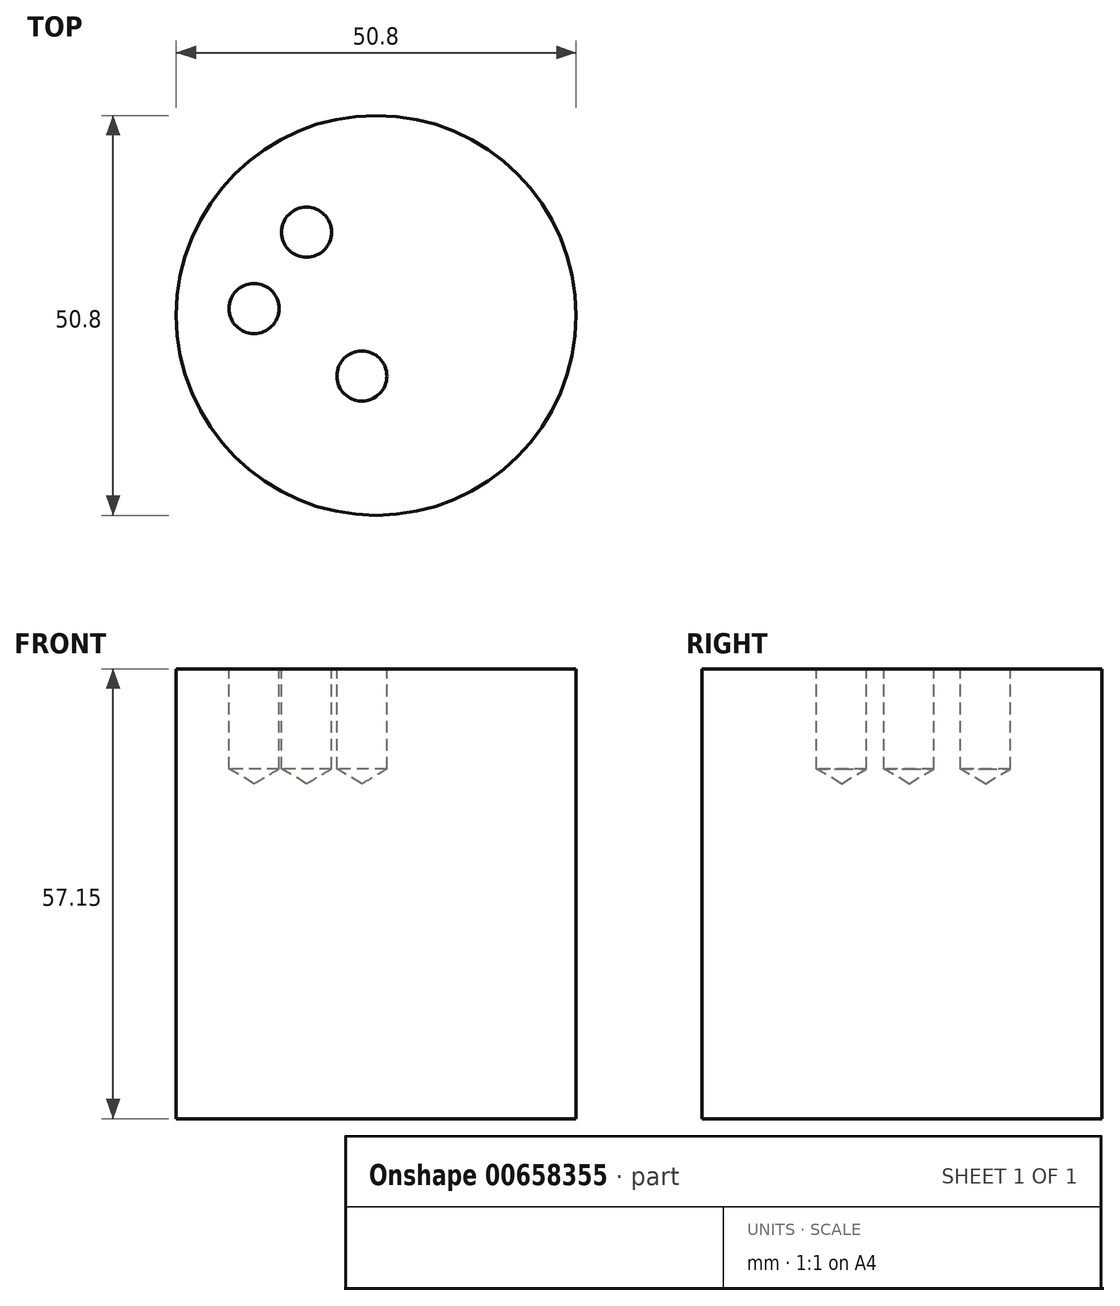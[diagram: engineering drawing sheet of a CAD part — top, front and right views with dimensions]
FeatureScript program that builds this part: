
annotation { "Feature Type Name" : "Feature", "Feature Type Description" : "" }
export const myFeature = defineFeature(function(context is Context, id is Id, definition is map)
    precondition{}
    {
        {
            var Q0;
            Q0=qCreatedBy(makeId("Top.planeOp"),FACE);
            var sketch = newSketch(context, id + "F0", { "sketchPlane" : qUnion([Q0])});
            skCircle(sketch, "E0", {"center": v(0, 0) * mm, "radius": 25.4 * mm});
            skSolve(sketch);
        }
        {
            var Q0;
            Q0=qCreatedBy(makeId("Top.planeOp"),FACE);
            cPlane(context, id + "F1", {"entities" : qUnion([Q0]), "cplaneType" : CPlaneType.OFFSET, "offset" : 57.15 * mm, "width" : 152.4 * mm, "height" : 152.4 * mm});
        }
        {
            var Q0;
            Q0 = qSketchRegion(id + "F0", true);
            var Q1;
            Q1=qCreatedBy(id+"F1.planeOp",FACE);
            extrude(context, id + "F2", {"entities" : qUnion([Q0]), "endBound" : BoundingType.UP_TO_SURFACE, "depth" : 25.4 * mm, "endBoundEntityFace" : qUnion([Q1]), "offsetDistance" : 25.4 * mm});
        }
        {
            var Q0;
            Q0=qCreatedBy(id+"F1.planeOp",FACE);
            var sketch = newSketch(context, id + "F3", { "sketchPlane" : qUnion([Q0])});
            skPoint(sketch, "E1", {"position": v(-15.51, 0.87) * mm});
            skPoint(sketch, "E2", {"position": v(-8.85, 10.56) * mm});
            skPoint(sketch, "E3", {"position": v(-1.82, -7.7) * mm});
            skSolve(sketch);
        }
        {
            var Q0;
            Q0=sQuery(id+"F3.wireOp",VERTEX,"E2");
            var Q1;
            Q1=sQuery(id+"F3.wireOp",VERTEX,"E1");
            var Q2;
            Q2=sQuery(id+"F3.wireOp",VERTEX,"E3");
            var Q3;
            Q3=makeQuery(id+"F2.opExtrude","SWEPT_BODY",BODY,{"disambiguationData":[OSD([sQuery(id+"F0.wireOp",EDGE,"E0")])]});
            hole(context, id + "F4", {"style" : HoleStyle.SIMPLE, "endStyle" : HoleEndStyle.BLIND, "holeDiameter" : 6.35 * mm, "majorDiameter" : 6.35 * mm, "holeDepth" : 12.7 * mm, "isTappedThrough" : true, "tappedDepth" : 12.7 * mm, "tapClearance" : 3, "locations" : qUnion([Q0, Q1, Q2]), "scope" : qUnion([Q3])});
        }
    });
